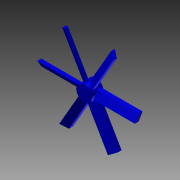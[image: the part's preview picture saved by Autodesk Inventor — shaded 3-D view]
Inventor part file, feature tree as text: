
AUTODESK INVENTOR PART (.ipt)
format: ipt  version: 2012 (Build 160160000, 160)  size: 121,856 bytes
history: native  units: mm
features: sketch x3, extrude x3, plane x1, pattern_circular x1
ambient origin geometry x8: Origin, YZ Plane, XZ Plane, XY Plane, X Axis, Y Axis, Z Axis, Center Point
bodies: Solid1 (feature_tree)
feature tree (8):
  sketch  "Sketch1"  dims[d0=1.5mm d1=8.0mm]
  extrude  "Extrusion1"  Depth=8.0mm
  extrude  "Extrusion2"  Depth=4.0mm TaperAngle=0.0deg
  plane  "Work Plane1"
  extrude  "Extrusion3"  TaperAngle=150.0deg  [1 undecoded]
  sketch  "Sketch3"  dims[d6=0.0mm d7=150.0deg d8=2.0mm d9=1.0mm d10=1.0mm d11=25.0mm d12=0.0mm d13=60.0mm d14=360.0deg]
  pattern_circular  "Circular Pattern1"  [2 undecoded]
  sketch  "Sketch2"  dims[d2=6.0mm d3=0.0mm d4=4.0mm d5=0.0mm]
note: 3 required parameter values undecoded (feature->parameter linkage not recoverable at this tier; creation-order binding heuristic only, values carry confidence <= 0.55)
